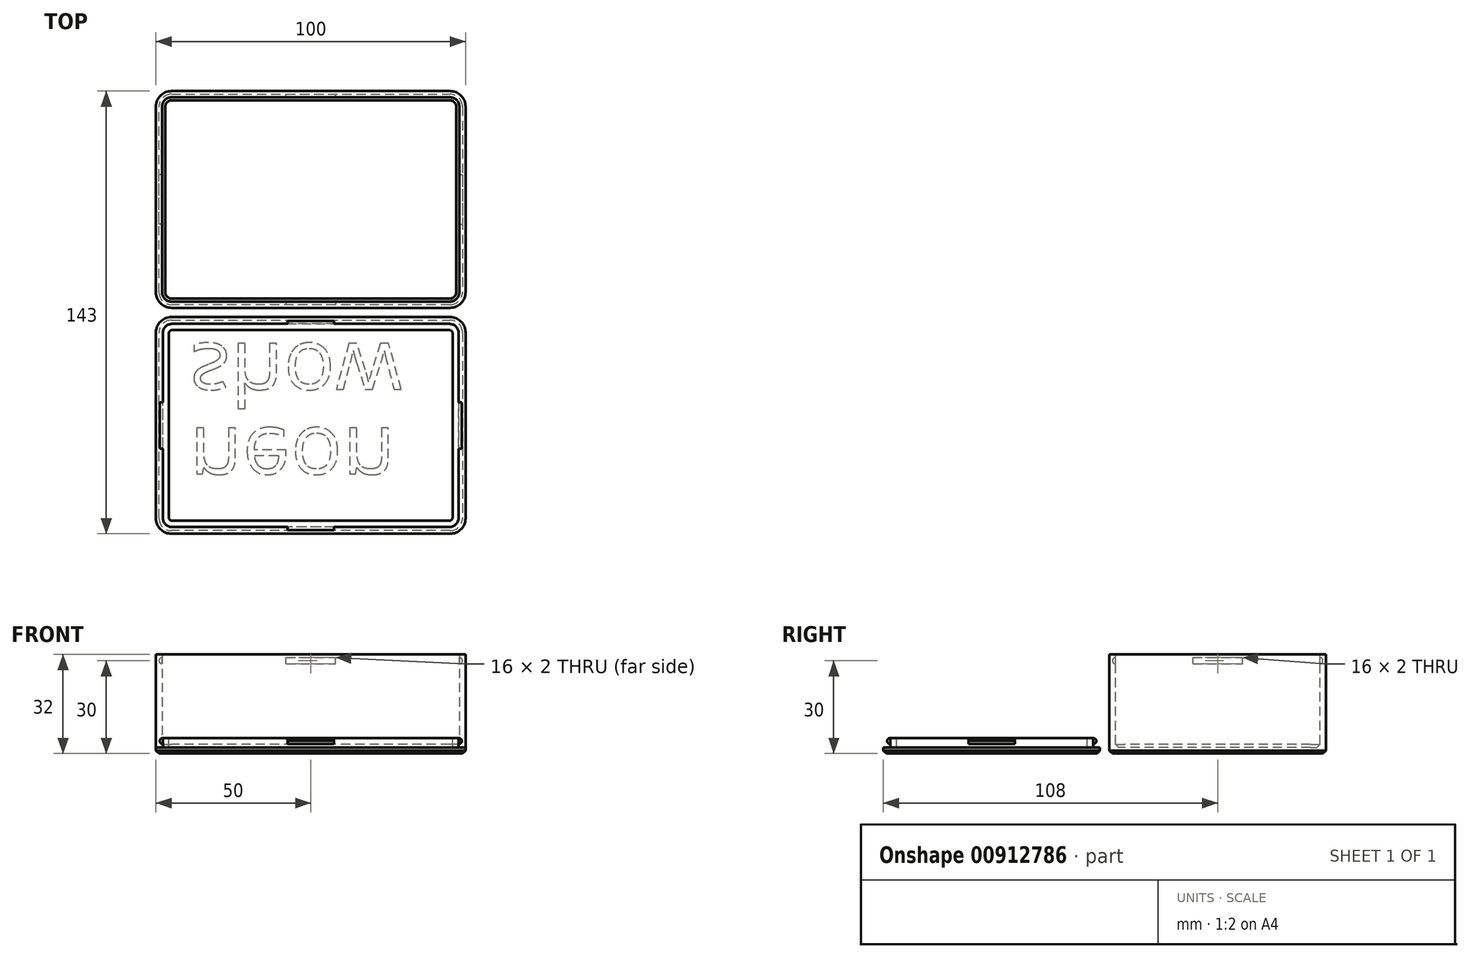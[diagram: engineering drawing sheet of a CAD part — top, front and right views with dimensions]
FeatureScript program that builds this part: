
annotation { "Feature Type Name" : "Feature", "Feature Type Description" : "" }
export const myFeature = defineFeature(function(context is Context, id is Id, definition is map)
    precondition{}
    {
        {
            assignVariable(context, id + "F0", {"name" : "box_height", "anyValue" : 30});
        }
        {
            var Q0;
            Q0=qCreatedBy(makeId("Top.planeOp"),FACE);
            var sketch = newSketch(context, id + "F1", { "sketchPlane" : qUnion([Q0])});
            skLineSegment(sketch, "E0.bottom", {"start": v(50, -35) * mm, "end": v(-50, -35) * mm});
            skLineSegment(sketch, "E0.top", {"start": v(50, 35) * mm, "end": v(-50, 35) * mm});
            skLineSegment(sketch, "E0.left", {"start": v(50, -35) * mm, "end": v(50, 35) * mm});
            skLineSegment(sketch, "E0.right", {"start": v(-50, -35) * mm, "end": v(-50, 35) * mm});
            skPoint(sketch, "E0.middle", {"position": v(0, 0) * mm});
            skLineSegment(sketch, "E1.bottom", {"start": v(50, -108) * mm, "end": v(-50, -108) * mm});
            skLineSegment(sketch, "E1.top", {"start": v(50, -38) * mm, "end": v(-50, -38) * mm});
            skLineSegment(sketch, "E1.left", {"start": v(50, -108) * mm, "end": v(50, -38) * mm});
            skLineSegment(sketch, "E1.right", {"start": v(-50, -108) * mm, "end": v(-50, -38) * mm});
            skPoint(sketch, "E1.middle", {"position": v(0, -73) * mm});
            skLineSegment(sketch, "E2.bottom", {"start": v(47.8, -105.8) * mm, "end": v(-47.8, -105.8) * mm});
            skLineSegment(sketch, "E2.top", {"start": v(47.8, -40.2) * mm, "end": v(-47.8, -40.2) * mm});
            skLineSegment(sketch, "E2.left", {"start": v(47.8, -105.8) * mm, "end": v(47.8, -40.2) * mm});
            skLineSegment(sketch, "E2.right", {"start": v(-47.8, -105.8) * mm, "end": v(-47.8, -40.2) * mm});
            skSolve(sketch);
        }
        {
            var Q0;
            Q0=makeQuery(id+"F1.imprint","IMPRINT",FACE,{"disambiguationData":[TD([[makeQuery(id+"F1.imprint","IMPRINT",EDGE,{"derivedFrom":sQuery(id+"F1.wireOp",EDGE,"E0.bottom")}),-1.0]])]});
            extrude(context, id + "F2", {"entities" : qUnion([Q0]), "oppositeDirection" : true, "depth" : 2 * mm, "offsetDistance" : 25 * mm});
        }
        {
            var Q0;
            Q0=makeQuery(id+"F2.opExtrude","CAP_FACE",FACE,{"disambiguationData":[OSD([sQuery(id+"F1.wireOp",EDGE,"E0.bottom"),sQuery(id+"F1.wireOp",EDGE,"E0.top"),sQuery(id+"F1.wireOp",EDGE,"E0.left"),sQuery(id+"F1.wireOp",EDGE,"E0.right")])],"isStart":true});
            extrude(context, id + "F3", {"entities" : qUnion([Q0]), "operationType" : NewBodyOperationType.ADD, "depth" : (getVariable(context, 'box_height')) * mm, "offsetDistance" : 25 * mm});
        }
        {
            var Q0;
            {var subQ0=sQuery(id+"F1.wireOp",EDGE,"E0.right");var subQ1=sQuery(id+"F1.wireOp",EDGE,"E0.top");Q0=makeQuery(id+"F3.boolean.opBoolean","MERGE",EDGE,{"derivedFrom":[makeQuery(id+"F2.opExtrude","SWEPT_EDGE",EDGE,{"disambiguationData":[OSD([subQ1,subQ0])]}),makeQuery(id+"F3.opExtrude","SWEPT_EDGE",EDGE,{"disambiguationData":[OSD([subQ1,subQ0])]})]});}
            var Q1;
            {var subQ0=sQuery(id+"F1.wireOp",EDGE,"E0.right");var subQ1=sQuery(id+"F1.wireOp",EDGE,"E0.bottom");Q1=makeQuery(id+"F3.boolean.opBoolean","MERGE",EDGE,{"derivedFrom":[makeQuery(id+"F2.opExtrude","SWEPT_EDGE",EDGE,{"disambiguationData":[OSD([subQ1,subQ0])]}),makeQuery(id+"F3.opExtrude","SWEPT_EDGE",EDGE,{"disambiguationData":[OSD([subQ1,subQ0])]})]});}
            var Q2;
            {var subQ0=sQuery(id+"F1.wireOp",EDGE,"E0.left");var subQ1=sQuery(id+"F1.wireOp",EDGE,"E0.bottom");Q2=makeQuery(id+"F3.boolean.opBoolean","MERGE",EDGE,{"derivedFrom":[makeQuery(id+"F2.opExtrude","SWEPT_EDGE",EDGE,{"disambiguationData":[OSD([subQ1,subQ0])]}),makeQuery(id+"F3.opExtrude","SWEPT_EDGE",EDGE,{"disambiguationData":[OSD([subQ1,subQ0])]})]});}
            var Q3;
            {var subQ0=sQuery(id+"F1.wireOp",EDGE,"E0.left");var subQ1=sQuery(id+"F1.wireOp",EDGE,"E0.top");Q3=makeQuery(id+"F3.boolean.opBoolean","MERGE",EDGE,{"derivedFrom":[makeQuery(id+"F2.opExtrude","SWEPT_EDGE",EDGE,{"disambiguationData":[OSD([subQ1,subQ0])]}),makeQuery(id+"F3.opExtrude","SWEPT_EDGE",EDGE,{"disambiguationData":[OSD([subQ1,subQ0])]})]});}
            fillet(context, id + "F4", {"entities" : qUnion([Q0, Q1, Q2, Q3]), "radius" : 5 * mm, "tangentPropagation" : true, "allowEdgeOverflow" : false});
        }
        {
            var Q0;
            Q0=makeQuery(id+"F3.opExtrude","CAP_FACE",FACE,{"disambiguationData":[OSD([sQuery(id+"F1.wireOp",EDGE,"E0.bottom"),sQuery(id+"F1.wireOp",EDGE,"E0.top"),sQuery(id+"F1.wireOp",EDGE,"E0.left"),sQuery(id+"F1.wireOp",EDGE,"E0.right")])],"isStart":false});
            shell(context, id + "F5", {"entities" : qUnion([Q0]), "thickness" : 2 * mm});
        }
        {
            var Q0;
            Q0=makeQuery(id+"F5.opShell","OFFSET_FACE",FACE,{"disambiguationData":[OSD([sQuery(id+"F1.wireOp",EDGE,"E0.right")])]});
            var sketch = newSketch(context, id + "F6", { "sketchPlane" : qUnion([Q0])});
            skLineSegment(sketch, "E3", {"start": v(0, 30) * mm, "end": v(0, 28) * mm});
            skPoint(sketch, "E3.endSnap0", {"position": v(0, 30) * mm});
            skLineSegment(sketch, "E4.bottom", {"start": v(8, 27) * mm, "end": v(-8, 27) * mm});
            skLineSegment(sketch, "E4.top", {"start": v(8, 29) * mm, "end": v(-8, 29) * mm});
            skLineSegment(sketch, "E4.left", {"start": v(8, 27) * mm, "end": v(8, 29) * mm});
            skLineSegment(sketch, "E4.right", {"start": v(-8, 27) * mm, "end": v(-8, 29) * mm});
            skPoint(sketch, "E4.middle", {"position": v(0, 28) * mm});
            skSolve(sketch);
        }
        {
            var Q0;
            Q0=makeQuery(id+"F5.opShell","OFFSET_FACE",FACE,{"disambiguationData":[OSD([sQuery(id+"F1.wireOp",EDGE,"E0.top")])]});
            var sketch = newSketch(context, id + "F7", { "sketchPlane" : qUnion([Q0])});
            skPoint(sketch, "E5", {"position": v(0, 30) * mm});
            skLineSegment(sketch, "E6", {"start": v(0, 30) * mm, "end": v(0, 28) * mm});
            skLineSegment(sketch, "E7.bottom", {"start": v(8, 27) * mm, "end": v(-8, 27) * mm});
            skLineSegment(sketch, "E7.top", {"start": v(8, 29) * mm, "end": v(-8, 29) * mm});
            skLineSegment(sketch, "E7.left", {"start": v(8, 27) * mm, "end": v(8, 29) * mm});
            skLineSegment(sketch, "E7.right", {"start": v(-8, 27) * mm, "end": v(-8, 29) * mm});
            skPoint(sketch, "E7.middle", {"position": v(0, 28) * mm});
            skSolve(sketch);
        }
        {
            var Q0;
            Q0=makeQuery(id+"F7.imprint","IMPRINT",FACE,{"disambiguationData":[TD([[makeQuery(id+"F7.imprint","IMPRINT",EDGE,{"derivedFrom":sQuery(id+"F7.wireOp",EDGE,"E7.bottom")}),-1.0]])]});
            extrude(context, id + "F8", {"entities" : qUnion([Q0]), "operationType" : NewBodyOperationType.REMOVE, "oppositeDirection" : true, "depth" : 1 * mm, "offsetDistance" : 25 * mm});
        }
        {
            var Q0;
            Q0=makeQuery(id+"F6.imprint","IMPRINT",FACE,{"disambiguationData":[TD([[makeQuery(id+"F6.imprint","IMPRINT",EDGE,{"derivedFrom":sQuery(id+"F6.wireOp",EDGE,"E4.bottom")}),-1.0]])]});
            extrude(context, id + "F9", {"entities" : qUnion([Q0]), "operationType" : NewBodyOperationType.REMOVE, "oppositeDirection" : true, "depth" : 1 * mm, "offsetDistance" : 25 * mm});
        }
        {
            var Q0;
            Q0=makeQuery(id+"F5.opShell","OFFSET_FACE",FACE,{"disambiguationData":[OSD([sQuery(id+"F1.wireOp",EDGE,"E0.bottom")])]});
            var sketch = newSketch(context, id + "F10", { "sketchPlane" : qUnion([Q0])});
            skLineSegment(sketch, "E8", {"start": v(0, 30) * mm, "end": v(0, 28) * mm});
            skPoint(sketch, "E8.endSnap0", {"position": v(0, 30) * mm});
            skLineSegment(sketch, "E9.bottom", {"start": v(8, 27) * mm, "end": v(-8, 27) * mm});
            skLineSegment(sketch, "E9.top", {"start": v(8, 29) * mm, "end": v(-8, 29) * mm});
            skLineSegment(sketch, "E9.left", {"start": v(8, 27) * mm, "end": v(8, 29) * mm});
            skLineSegment(sketch, "E9.right", {"start": v(-8, 27) * mm, "end": v(-8, 29) * mm});
            skPoint(sketch, "E9.middle", {"position": v(0, 28) * mm});
            skSolve(sketch);
        }
        {
            var Q0;
            Q0=makeQuery(id+"F10.imprint","IMPRINT",FACE,{"disambiguationData":[TD([[makeQuery(id+"F10.imprint","IMPRINT",EDGE,{"derivedFrom":sQuery(id+"F10.wireOp",EDGE,"E9.bottom")}),-1.0]])]});
            extrude(context, id + "F11", {"entities" : qUnion([Q0]), "operationType" : NewBodyOperationType.REMOVE, "oppositeDirection" : true, "depth" : 1 * mm, "offsetDistance" : 25 * mm});
        }
        {
            var Q0;
            Q0=makeQuery(id+"F5.opShell","OFFSET_FACE",FACE,{"disambiguationData":[OSD([sQuery(id+"F1.wireOp",EDGE,"E0.left")])]});
            var sketch = newSketch(context, id + "F12", { "sketchPlane" : qUnion([Q0])});
            skLineSegment(sketch, "E10", {"start": v(0, 30) * mm, "end": v(0, 28) * mm});
            skPoint(sketch, "E10.endSnap0", {"position": v(0, 30) * mm});
            skLineSegment(sketch, "E11.bottom", {"start": v(8, 27) * mm, "end": v(-8, 27) * mm});
            skLineSegment(sketch, "E11.top", {"start": v(8, 29) * mm, "end": v(-8, 29) * mm});
            skLineSegment(sketch, "E11.left", {"start": v(8, 27) * mm, "end": v(8, 29) * mm});
            skLineSegment(sketch, "E11.right", {"start": v(-8, 27) * mm, "end": v(-8, 29) * mm});
            skPoint(sketch, "E11.middle", {"position": v(0, 28) * mm});
            skSolve(sketch);
        }
        {
            var Q0;
            Q0=makeQuery(id+"F12.imprint","IMPRINT",FACE,{"disambiguationData":[TD([[makeQuery(id+"F12.imprint","IMPRINT",EDGE,{"derivedFrom":sQuery(id+"F12.wireOp",EDGE,"E11.bottom")}),-1.0]])]});
            extrude(context, id + "F13", {"entities" : qUnion([Q0]), "operationType" : NewBodyOperationType.REMOVE, "oppositeDirection" : true, "depth" : 1 * mm, "offsetDistance" : 25 * mm});
        }
        {
            var Q0;
            Q0=makeQuery(id+"F1.imprint","IMPRINT",FACE,{"disambiguationData":[TD([[makeQuery(id+"F1.imprint","IMPRINT",EDGE,{"derivedFrom":sQuery(id+"F1.wireOp",EDGE,"E1.bottom")}),-1.0]])]});
            var Q1;
            Q1=makeQuery(id+"F1.imprint","IMPRINT",FACE,{"disambiguationData":[TD([[makeQuery(id+"F1.imprint","IMPRINT",EDGE,{"derivedFrom":sQuery(id+"F1.wireOp",EDGE,"E2.bottom")}),-1.0]])]});
            var Q2;
            Q2=makeQuery(id+"F1.imprint","IMPRINT",FACE,{"disambiguationData":[TD([[makeQuery(id+"F1.imprint","IMPRINT",EDGE,{"derivedFrom":sQuery(id+"F1.wireOp",EDGE,"IM9Et3MU-YbXc-tv5d-9tDR-dDhzX9vFgJBc.bottom")}),-1.0]])]});
            extrude(context, id + "F14", {"entities" : qUnion([Q0, Q1, Q2]), "oppositeDirection" : true, "depth" : 2 * mm, "offsetDistance" : 25 * mm});
        }
        {
            var Q0;
            Q0=makeQuery(id+"F14.opExtrude","SWEPT_EDGE",EDGE,{"disambiguationData":[OSD([sQuery(id+"F1.wireOp",EDGE,"E1.bottom"),sQuery(id+"F1.wireOp",EDGE,"E1.right")])]});
            var Q1;
            Q1=makeQuery(id+"F14.opExtrude","SWEPT_EDGE",EDGE,{"disambiguationData":[OSD([sQuery(id+"F1.wireOp",EDGE,"E1.top"),sQuery(id+"F1.wireOp",EDGE,"E1.right")])]});
            var Q2;
            Q2=makeQuery(id+"F14.opExtrude","SWEPT_EDGE",EDGE,{"disambiguationData":[OSD([sQuery(id+"F1.wireOp",EDGE,"E1.bottom"),sQuery(id+"F1.wireOp",EDGE,"E1.left")])]});
            var Q3;
            Q3=makeQuery(id+"F14.opExtrude","SWEPT_EDGE",EDGE,{"disambiguationData":[OSD([sQuery(id+"F1.wireOp",EDGE,"E1.top"),sQuery(id+"F1.wireOp",EDGE,"E1.left")])]});
            fillet(context, id + "F15", {"entities" : qUnion([Q0, Q1, Q2, Q3]), "radius" : 5 * mm, "tangentPropagation" : true, "allowEdgeOverflow" : false});
        }
        {
            var Q0;
            Q0=makeQuery(id+"F1.imprint","IMPRINT",FACE,{"disambiguationData":[TD([[makeQuery(id+"F1.imprint","IMPRINT",EDGE,{"derivedFrom":sQuery(id+"F1.wireOp",EDGE,"E2.bottom")}),-1.0]])]});
            extrude(context, id + "F16", {"entities" : qUnion([Q0]), "operationType" : NewBodyOperationType.ADD, "depth" : 3 * mm, "offsetDistance" : 25 * mm});
        }
        {
            var Q0;
            Q0=makeQuery(id+"F16.opExtrude","SWEPT_EDGE",EDGE,{"disambiguationData":[OSD([sQuery(id+"F1.wireOp",EDGE,"E2.bottom"),sQuery(id+"F1.wireOp",EDGE,"E2.right")])]});
            var Q1;
            Q1=makeQuery(id+"F16.opExtrude","SWEPT_EDGE",EDGE,{"disambiguationData":[OSD([sQuery(id+"F1.wireOp",EDGE,"E2.bottom"),sQuery(id+"F1.wireOp",EDGE,"E2.left")])]});
            var Q2;
            Q2=makeQuery(id+"F16.opExtrude","SWEPT_EDGE",EDGE,{"disambiguationData":[OSD([sQuery(id+"F1.wireOp",EDGE,"E2.top"),sQuery(id+"F1.wireOp",EDGE,"E2.left")])]});
            var Q3;
            Q3=makeQuery(id+"F16.opExtrude","SWEPT_EDGE",EDGE,{"disambiguationData":[OSD([sQuery(id+"F1.wireOp",EDGE,"E2.top"),sQuery(id+"F1.wireOp",EDGE,"E2.right")])]});
            fillet(context, id + "F17", {"entities" : qUnion([Q0, Q1, Q2, Q3]), "radius" : 3 * mm, "tangentPropagation" : true, "allowEdgeOverflow" : false});
        }
        {
            var Q0;
            Q0=makeQuery(id+"F16.opExtrude","CAP_FACE",FACE,{"disambiguationData":[OSD([sQuery(id+"F1.wireOp",EDGE,"E2.bottom"),sQuery(id+"F1.wireOp",EDGE,"E2.top"),sQuery(id+"F1.wireOp",EDGE,"E2.left"),sQuery(id+"F1.wireOp",EDGE,"E2.right")])],"isStart":false});
            shell(context, id + "F18", {"entities" : qUnion([Q0]), "thickness" : 2 * mm});
        }
        {
            var Q0;
            Q0=makeQuery(id+"F16.opExtrude","SWEPT_FACE",FACE,{"disambiguationData":[OSD([sQuery(id+"F1.wireOp",EDGE,"E2.bottom")])]});
            var sketch = newSketch(context, id + "F19", { "sketchPlane" : qUnion([Q0])});
            skLineSegment(sketch, "E12", {"start": v(0, 3) * mm, "end": v(0, 2.05) * mm});
            skPoint(sketch, "E12.endSnap0", {"position": v(0, 3) * mm});
            skLineSegment(sketch, "E13.bottom", {"start": v(7.5, 1.1) * mm, "end": v(-7.5, 1.1) * mm});
            skLineSegment(sketch, "E13.top", {"start": v(7.5, 3) * mm, "end": v(-7.5, 3) * mm});
            skLineSegment(sketch, "E13.left", {"start": v(7.5, 1.1) * mm, "end": v(7.5, 3) * mm});
            skLineSegment(sketch, "E13.right", {"start": v(-7.5, 1.1) * mm, "end": v(-7.5, 3) * mm});
            skPoint(sketch, "E13.middle", {"position": v(0, 2.05) * mm});
            skSolve(sketch);
        }
        {
            var Q0;
            Q0=makeQuery(id+"F19.imprint","IMPRINT",FACE,{"disambiguationData":[TD([[makeQuery(id+"F19.imprint","IMPRINT",EDGE,{"derivedFrom":sQuery(id+"F19.wireOp",EDGE,"E13.bottom")}),-1.0]])]});
            extrude(context, id + "F20", {"entities" : qUnion([Q0]), "operationType" : NewBodyOperationType.ADD, "depth" : 1 * mm, "offsetDistance" : 25 * mm});
        }
        {
            var Q0;
            Q0=makeQuery(id+"F16.opExtrude","SWEPT_FACE",FACE,{"disambiguationData":[OSD([sQuery(id+"F1.wireOp",EDGE,"E2.right")])]});
            var sketch = newSketch(context, id + "F21", { "sketchPlane" : qUnion([Q0])});
            skLineSegment(sketch, "E14", {"start": v(73, 3) * mm, "end": v(73, 2.05) * mm});
            skLineSegment(sketch, "E15.bottom", {"start": v(80.5, 1.1) * mm, "end": v(65.5, 1.1) * mm});
            skLineSegment(sketch, "E15.top", {"start": v(80.5, 3) * mm, "end": v(65.5, 3) * mm});
            skLineSegment(sketch, "E15.left", {"start": v(80.5, 1.1) * mm, "end": v(80.5, 3) * mm});
            skLineSegment(sketch, "E15.right", {"start": v(65.5, 1.1) * mm, "end": v(65.5, 3) * mm});
            skPoint(sketch, "E15.middle", {"position": v(73, 2.05) * mm});
            skSolve(sketch);
        }
        {
            var Q0;
            Q0=makeQuery(id+"F21.imprint","IMPRINT",FACE,{"disambiguationData":[TD([[makeQuery(id+"F21.imprint","IMPRINT",EDGE,{"derivedFrom":sQuery(id+"F21.wireOp",EDGE,"E15.bottom")}),-1.0]])]});
            extrude(context, id + "F22", {"entities" : qUnion([Q0]), "operationType" : NewBodyOperationType.ADD, "depth" : 1 * mm, "offsetDistance" : 25 * mm});
        }
        {
            var Q0;
            Q0=makeQuery(id+"F16.opExtrude","SWEPT_FACE",FACE,{"disambiguationData":[OSD([sQuery(id+"F1.wireOp",EDGE,"E2.left")])]});
            var sketch = newSketch(context, id + "F23", { "sketchPlane" : qUnion([Q0])});
            skLineSegment(sketch, "E16", {"start": v(-73, 3) * mm, "end": v(-73, 2.05) * mm});
            skLineSegment(sketch, "E17.bottom", {"start": v(-65.5, 1.1) * mm, "end": v(-80.5, 1.1) * mm});
            skLineSegment(sketch, "E17.top", {"start": v(-65.5, 3) * mm, "end": v(-80.5, 3) * mm});
            skLineSegment(sketch, "E17.left", {"start": v(-65.5, 1.1) * mm, "end": v(-65.5, 3) * mm});
            skLineSegment(sketch, "E17.right", {"start": v(-80.5, 1.1) * mm, "end": v(-80.5, 3) * mm});
            skPoint(sketch, "E17.middle", {"position": v(-73, 2.05) * mm});
            skSolve(sketch);
        }
        {
            var Q0;
            Q0=makeQuery(id+"F23.imprint","IMPRINT",FACE,{"disambiguationData":[TD([[makeQuery(id+"F23.imprint","IMPRINT",EDGE,{"derivedFrom":sQuery(id+"F23.wireOp",EDGE,"E17.bottom")}),-1.0]])]});
            extrude(context, id + "F24", {"entities" : qUnion([Q0]), "operationType" : NewBodyOperationType.ADD, "depth" : 1 * mm, "offsetDistance" : 25 * mm});
        }
        {
            var Q0;
            Q0=makeQuery(id+"F16.opExtrude","SWEPT_FACE",FACE,{"disambiguationData":[OSD([sQuery(id+"F1.wireOp",EDGE,"E2.top")])]});
            var sketch = newSketch(context, id + "F25", { "sketchPlane" : qUnion([Q0])});
            skLineSegment(sketch, "E18", {"start": v(0, 3) * mm, "end": v(0, 2.05) * mm});
            skPoint(sketch, "E18.endSnap0", {"position": v(0, 3) * mm});
            skLineSegment(sketch, "E19.bottom", {"start": v(7.5, 1.1) * mm, "end": v(-7.5, 1.1) * mm});
            skLineSegment(sketch, "E19.top", {"start": v(7.5, 3) * mm, "end": v(-7.5, 3) * mm});
            skLineSegment(sketch, "E19.left", {"start": v(7.5, 1.1) * mm, "end": v(7.5, 3) * mm});
            skLineSegment(sketch, "E19.right", {"start": v(-7.5, 1.1) * mm, "end": v(-7.5, 3) * mm});
            skPoint(sketch, "E19.middle", {"position": v(0, 2.05) * mm});
            skSolve(sketch);
        }
        {
            var Q0;
            Q0=makeQuery(id+"F25.imprint","IMPRINT",FACE,{"disambiguationData":[TD([[makeQuery(id+"F25.imprint","IMPRINT",EDGE,{"derivedFrom":sQuery(id+"F25.wireOp",EDGE,"E19.bottom")}),-1.0]])]});
            extrude(context, id + "F26", {"entities" : qUnion([Q0]), "operationType" : NewBodyOperationType.ADD, "depth" : 1 * mm, "offsetDistance" : 25 * mm});
        }
        {
            var Q0;
            Q0=makeQuery(id+"F8.boolean.opBoolean","COPY",EDGE,{"derivedFrom":makeQuery(id+"F8.opExtrude","CAP_EDGE",EDGE,{"disambiguationData":[OSD([sQuery(id+"F7.wireOp",EDGE,"E7.bottom")])],"isStart":false})});
            var Q1;
            Q1=makeQuery(id+"F8.boolean.opBoolean","COPY",EDGE,{"derivedFrom":makeQuery(id+"F8.opExtrude","CAP_EDGE",EDGE,{"disambiguationData":[OSD([sQuery(id+"F7.wireOp",EDGE,"E7.top")])],"isStart":false})});
            var Q2;
            Q2=makeQuery(id+"F13.boolean.opBoolean","COPY",EDGE,{"derivedFrom":makeQuery(id+"F13.opExtrude","CAP_EDGE",EDGE,{"disambiguationData":[OSD([sQuery(id+"F12.wireOp",EDGE,"E11.bottom")])],"isStart":false})});
            var Q3;
            Q3=makeQuery(id+"F13.boolean.opBoolean","COPY",EDGE,{"derivedFrom":makeQuery(id+"F13.opExtrude","CAP_EDGE",EDGE,{"disambiguationData":[OSD([sQuery(id+"F12.wireOp",EDGE,"E11.top")])],"isStart":false})});
            var Q4;
            Q4=makeQuery(id+"F11.boolean.opBoolean","COPY",EDGE,{"derivedFrom":makeQuery(id+"F11.opExtrude","CAP_EDGE",EDGE,{"disambiguationData":[OSD([sQuery(id+"F10.wireOp",EDGE,"E9.bottom")])],"isStart":false})});
            var Q5;
            Q5=makeQuery(id+"F11.boolean.opBoolean","COPY",EDGE,{"derivedFrom":makeQuery(id+"F11.opExtrude","CAP_EDGE",EDGE,{"disambiguationData":[OSD([sQuery(id+"F10.wireOp",EDGE,"E9.top")])],"isStart":false})});
            var Q6;
            Q6=makeQuery(id+"F9.boolean.opBoolean","COPY",EDGE,{"derivedFrom":makeQuery(id+"F9.opExtrude","CAP_EDGE",EDGE,{"disambiguationData":[OSD([sQuery(id+"F6.wireOp",EDGE,"E4.bottom")])],"isStart":false})});
            var Q7;
            Q7=makeQuery(id+"F9.boolean.opBoolean","COPY",EDGE,{"derivedFrom":makeQuery(id+"F9.opExtrude","CAP_EDGE",EDGE,{"disambiguationData":[OSD([sQuery(id+"F6.wireOp",EDGE,"E4.top")])],"isStart":false})});
            var Q8;
            Q8=makeQuery(id+"F26.opExtrude","CAP_EDGE",EDGE,{"disambiguationData":[OSD([sQuery(id+"F25.wireOp",EDGE,"E19.top")])],"isStart":false});
            var Q9;
            Q9=makeQuery(id+"F26.opExtrude","CAP_EDGE",EDGE,{"disambiguationData":[OSD([sQuery(id+"F25.wireOp",EDGE,"E19.bottom")])],"isStart":false});
            var Q10;
            Q10=makeQuery(id+"F24.opExtrude","CAP_EDGE",EDGE,{"disambiguationData":[OSD([sQuery(id+"F23.wireOp",EDGE,"E17.bottom")])],"isStart":false});
            var Q11;
            Q11=makeQuery(id+"F24.opExtrude","CAP_EDGE",EDGE,{"disambiguationData":[OSD([sQuery(id+"F23.wireOp",EDGE,"E17.top")])],"isStart":false});
            var Q12;
            Q12=makeQuery(id+"F20.opExtrude","CAP_EDGE",EDGE,{"disambiguationData":[OSD([sQuery(id+"F19.wireOp",EDGE,"E13.bottom")])],"isStart":false});
            var Q13;
            Q13=makeQuery(id+"F20.opExtrude","CAP_EDGE",EDGE,{"disambiguationData":[OSD([sQuery(id+"F19.wireOp",EDGE,"E13.top")])],"isStart":false});
            var Q14;
            Q14=makeQuery(id+"F22.opExtrude","CAP_EDGE",EDGE,{"disambiguationData":[OSD([sQuery(id+"F21.wireOp",EDGE,"E15.bottom")])],"isStart":false});
            var Q15;
            Q15=makeQuery(id+"F22.opExtrude","CAP_EDGE",EDGE,{"disambiguationData":[OSD([sQuery(id+"F21.wireOp",EDGE,"E15.top")])],"isStart":false});
            fillet(context, id + "F27", {"entities" : qUnion([Q0, Q1, Q2, Q3, Q4, Q5, Q6, Q7, Q8, Q9, Q10, Q11, Q12, Q13, Q14, Q15]), "radius" : 1 * mm, "tangentPropagation" : true, "allowEdgeOverflow" : false});
        }
        {
            var Q0;
            Q0=makeQuery(id+"F14.opExtrude","CAP_FACE",FACE,{"disambiguationData":[OSD([sQuery(id+"F1.wireOp",EDGE,"E1.bottom"),sQuery(id+"F1.wireOp",EDGE,"E1.top"),sQuery(id+"F1.wireOp",EDGE,"E1.left"),sQuery(id+"F1.wireOp",EDGE,"E1.right")])],"isStart":false});
            var sketch = newSketch(context, id + "F28", { "sketchPlane" : qUnion([Q0])});
            skText(sketch, "E20", { "text": "neon", "fontName": "OpenSans-Regular.ttf"});
            skText(sketch, "E21", { "text": "show", "fontName": "OpenSans-Regular.ttf"});
            const initialGuessF28  = {"E20": [-0.03915, 0.07383, 1, 0, 0.02], "E21": [-0.03915, 0.04649, 1, 0, 0.02]};
            skSetInitialGuess(sketch, initialGuessF28);
            skSolve(sketch);
        }
        {
            var Q0;
            Q0=qSketchRegion(id+"F28",true);
            extrude(context, id + "F29", {"entities" : qUnion([Q0]), "operationType" : NewBodyOperationType.REMOVE, "oppositeDirection" : true, "depth" : 1 * mm, "offsetDistance" : 25 * mm});
        }
        {
            var Q0;
            Q0=makeQuery(id+"F2.opExtrude","CAP_EDGE",EDGE,{"disambiguationData":[OSD([sQuery(id+"F1.wireOp",EDGE,"E0.bottom")])],"isStart":false});
            var Q1;
            {var subQ1=sQuery(id+"F1.wireOp",EDGE,"E0.top");Q1=makeQuery(id+"FpG9AQefOrxavex_1.boolean.opBoolean","SPLIT",EDGE,{"disambiguationData":[TD([makeQuery(id+"FpG9AQefOrxavex_1.opExtrude","SWEPT_FACE",FACE,{"disambiguationData":[OSD([sQuery(id+"FlhJuv6juqtCqgM_1.wireOp",EDGE,"owPXrvsi-LDb6-3W9j-WWKj-u5mYioUlMwPM")])]})])],"derivedFrom":makeQuery(id+"F5.opShell","OFFSET_EDGE",EDGE,{"disambiguationData":[OSD([subQ1]),TDD([makeQuery(id+"F2.opExtrude","CAP_EDGE",EDGE,{"disambiguationData":[OSD([subQ1])],"isStart":false})])]})});}
            var Q2;
            {var subQ1=sQuery(id+"F1.wireOp",EDGE,"E0.bottom");var subQ4=makeQuery(id+"FpG9AQefOrxavex_1.opExtrude","SWEPT_FACE",FACE,{"disambiguationData":[OSD([sQuery(id+"FlhJuv6juqtCqgM_1.wireOp",EDGE,"owPXrvsi-LDb6-3W9j-WWKj-u5mYioUlMwPM")])]});Q2=makeQuery(id+"FuhzWpI5D5ixYZy_1.boolean.opBoolean","SPLIT",EDGE,{"disambiguationData":[TD([subQ4])],"derivedFrom":makeQuery(id+"FpG9AQefOrxavex_1.boolean.opBoolean","SPLIT",EDGE,{"disambiguationData":[TD([subQ4])],"derivedFrom":makeQuery(id+"F5.opShell","OFFSET_EDGE",EDGE,{"disambiguationData":[OSD([subQ1]),TDD([makeQuery(id+"F2.opExtrude","CAP_EDGE",EDGE,{"disambiguationData":[OSD([subQ1])],"isStart":false})])]})})});}
            var Q3;
            {var subQ1=sQuery(id+"F1.wireOp",EDGE,"E0.bottom");Q3=makeQuery(id+"FuhzWpI5D5ixYZy_1.boolean.opBoolean","SPLIT",EDGE,{"disambiguationData":[TD([makeQuery(id+"Fk2dAVFD3k9iBku_1.opExtrude","SWEPT_FACE",FACE,{"disambiguationData":[OSD([sQuery(id+"FlhJuv6juqtCqgM_1.wireOp",EDGE,"knURG02E-BIlg-6fKE-9kPn-FntDPsJJA3Fl")])]})])],"derivedFrom":makeQuery(id+"FpG9AQefOrxavex_1.boolean.opBoolean","SPLIT",EDGE,{"disambiguationData":[TD([makeQuery(id+"FpG9AQefOrxavex_1.opExtrude","SWEPT_FACE",FACE,{"disambiguationData":[OSD([sQuery(id+"FlhJuv6juqtCqgM_1.wireOp",EDGE,"owPXrvsi-LDb6-3W9j-WWKj-u5mYioUlMwPM")])]})])],"derivedFrom":makeQuery(id+"F5.opShell","OFFSET_EDGE",EDGE,{"disambiguationData":[OSD([subQ1]),TDD([makeQuery(id+"F2.opExtrude","CAP_EDGE",EDGE,{"disambiguationData":[OSD([subQ1])],"isStart":false})])]})})});}
            var Q4;
            {var subQ1=sQuery(id+"F1.wireOp",EDGE,"E0.bottom");Q4=makeQuery(id+"FpG9AQefOrxavex_1.boolean.opBoolean","SPLIT",EDGE,{"disambiguationData":[TD([makeQuery(id+"FpG9AQefOrxavex_1.opExtrude","SWEPT_FACE",FACE,{"disambiguationData":[OSD([sQuery(id+"FlhJuv6juqtCqgM_1.wireOp",EDGE,"pD2LKGx1-45yq-9jYG-vU1i-ZOhrXTbbIUP5")])]})])],"derivedFrom":makeQuery(id+"F5.opShell","OFFSET_EDGE",EDGE,{"disambiguationData":[OSD([subQ1]),TDD([makeQuery(id+"F2.opExtrude","CAP_EDGE",EDGE,{"disambiguationData":[OSD([subQ1])],"isStart":false})])]})});}
            var Q5;
            Q5=makeQuery(id+"F14.opExtrude","CAP_EDGE",EDGE,{"disambiguationData":[OSD([sQuery(id+"F1.wireOp",EDGE,"E1.bottom")])],"isStart":false});
            chamfer(context, id + "F30", {"entities" : qUnion([Q0, Q1, Q2, Q3, Q4, Q5]), "width" : 1 * mm, "tangentPropagation" : true});
        }
    });
